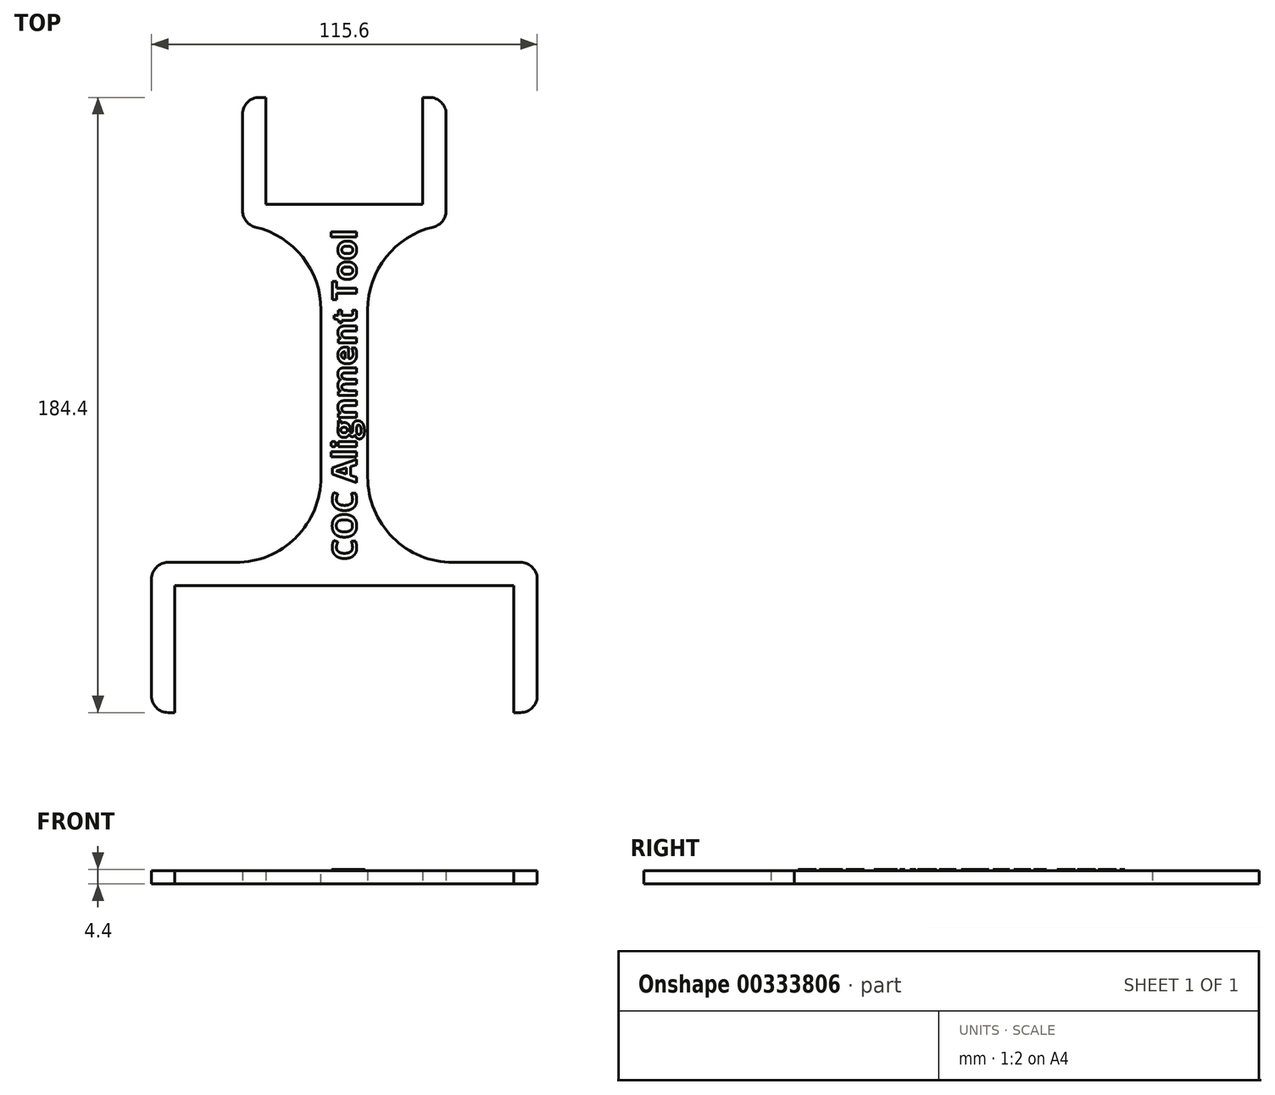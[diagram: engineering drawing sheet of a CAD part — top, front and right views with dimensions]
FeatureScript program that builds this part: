
annotation { "Feature Type Name" : "Feature", "Feature Type Description" : "" }
export const myFeature = defineFeature(function(context is Context, id is Id, definition is map)
    precondition{}
    {
        {
            var Q0;
            Q0=qCreatedBy(makeId("Top.planeOp"),FACE);
            var sketch = newSketch(context, id + "F0", { "sketchPlane" : qUnion([Q0])});
            skLineSegment(sketch, "E0", {"start": v(0, 0) * mm, "end": v(0, -57.2) * mm, "construction": true});
            skLineSegment(sketch, "E1", {"start": v(-50.8, -57.2) * mm, "end": v(50.8, -57.2) * mm});
            skLineSegment(sketch, "E2", {"start": v(-50.8, -57.2) * mm, "end": v(-50.8, -95.2) * mm});
            skLineSegment(sketch, "E3", {"start": v(50.8, -57.2) * mm, "end": v(50.8, -95.2) * mm});
            skLineSegment(sketch, "E4", {"start": v(0, 0) * mm, "end": v(0, 57.2) * mm, "construction": true});
            skLineSegment(sketch, "E5", {"start": v(-23.5, 57.2) * mm, "end": v(23.5, 57.2) * mm});
            skLineSegment(sketch, "E6", {"start": v(-23.5, 57.2) * mm, "end": v(-23.5, 89.2) * mm});
            skLineSegment(sketch, "E7", {"start": v(23.5, 57.2) * mm, "end": v(23.5, 89.2) * mm});
            skLineSegment(sketch, "E8", {"start": v(23.5, 89.2) * mm, "end": v(30.5, 89.2) * mm});
            skLineSegment(sketch, "E9", {"start": v(30.5, 89.2) * mm, "end": v(30.5, 57.2) * mm});
            skLineSegment(sketch, "E10", {"start": v(-23.5, 89.2) * mm, "end": v(-30.5, 89.2) * mm});
            skLineSegment(sketch, "E11", {"start": v(-50.8, -95.2) * mm, "end": v(-57.8, -95.2) * mm});
            skLineSegment(sketch, "E12", {"start": v(50.8, -95.2) * mm, "end": v(57.8, -95.2) * mm});
            skLineSegment(sketch, "E13", {"start": v(57.8, -95.2) * mm, "end": v(57.8, -57.2) * mm});
            skLineSegment(sketch, "E14", {"start": v(-57.8, -95.2) * mm, "end": v(-57.8, -57.2) * mm});
            skLineSegment(sketch, "E15", {"start": v(-30.5, 89.2) * mm, "end": v(-30.5, 57.2) * mm});
            skLineSegment(sketch, "E16", {"start": v(-30.5, 57.2) * mm, "end": v(-30.5, 50.2) * mm});
            skLineSegment(sketch, "E17", {"start": v(0, 50.2) * mm, "end": v(-7, 50.2) * mm, "construction": true});
            skLineSegment(sketch, "E18", {"start": v(-30.5, 50.2) * mm, "end": v(-7, 50.2) * mm});
            skLineSegment(sketch, "E19", {"start": v(0, 50.2) * mm, "end": v(7, 50.2) * mm, "construction": true});
            skLineSegment(sketch, "E20", {"start": v(7, 50.2) * mm, "end": v(30.5, 50.2) * mm});
            skLineSegment(sketch, "E21", {"start": v(30.5, 50.2) * mm, "end": v(30.5, 57.2) * mm});
            skLineSegment(sketch, "E22", {"start": v(-57.8, -57.2) * mm, "end": v(-57.8, -50.2) * mm});
            skLineSegment(sketch, "E23", {"start": v(-57.8, -50.2) * mm, "end": v(-7, -50.2) * mm});
            skLineSegment(sketch, "E24", {"start": v(-7, -50.2) * mm, "end": v(-7, 50.2) * mm});
            skLineSegment(sketch, "E25", {"start": v(57.8, -57.2) * mm, "end": v(57.8, -50.2) * mm});
            skLineSegment(sketch, "E26", {"start": v(57.8, -50.2) * mm, "end": v(7, -50.2) * mm});
            skLineSegment(sketch, "E27", {"start": v(7, -50.2) * mm, "end": v(7, 50.2) * mm});
            skLineSegment(sketch, "E28", {"start": v(-7, -50.2) * mm, "end": v(-22, -50.2) * mm, "construction": true});
            skLineSegment(sketch, "E29", {"start": v(-7, -50.2) * mm, "end": v(-7, -35.2) * mm, "construction": true});
            skLineSegment(sketch, "E30", {"start": v(-22, -50.2) * mm, "end": v(-7, -35.2) * mm});
            skLineSegment(sketch, "E31.MirrorCS", {"start": v(22, -50.2) * mm, "end": v(7, -35.2) * mm});
            skSolve(sketch);
        }
        {
            var Q0;
            Q0=makeQuery(id+"F0.imprint","IMPRINT",FACE,{"disambiguationData":[TD([[makeQuery(id+"F0.imprint","IMPRINT",EDGE,{"derivedFrom":sQuery(id+"F0.wireOp",EDGE,"E1")}),1.0]])]});
            var Q1;
            {var subQ3=sQuery(id+"F0.wireOp",EDGE,"E30");Q1=makeQuery(id+"F0.imprint","IMPRINT",FACE,{"disambiguationData":[TD([[makeQuery(id+"F0.imprint","IMPRINT",EDGE,{"derivedFrom":subQ3}),-1.0]])]});}
            var Q2;
            {var subQ3=sQuery(id+"F0.wireOp",EDGE,"E31.MirrorCS");Q2=makeQuery(id+"F0.imprint","IMPRINT",FACE,{"disambiguationData":[TD([[makeQuery(id+"F0.imprint","IMPRINT",EDGE,{"derivedFrom":subQ3}),1.0]])]});}
            extrude(context, id + "F1", {"entities" : qUnion([Q0, Q1, Q2]), "depth" : 4 * mm});
        }
        {
            var Q0;
            Q0=makeQuery(id+"F1.opExtrude","SWEPT_EDGE",EDGE,{"disambiguationData":[OSD([sQuery(id+"F0.wireOp",EDGE,"E22"),sQuery(id+"F0.wireOp",EDGE,"E23")])]});
            var Q1;
            Q1=makeQuery(id+"F1.opExtrude","SWEPT_EDGE",EDGE,{"disambiguationData":[OSD([sQuery(id+"F0.wireOp",EDGE,"E25"),sQuery(id+"F0.wireOp",EDGE,"E26")])]});
            var Q2;
            Q2=makeQuery(id+"F1.opExtrude","SWEPT_EDGE",EDGE,{"disambiguationData":[OSD([sQuery(id+"F0.wireOp",EDGE,"E20"),sQuery(id+"F0.wireOp",EDGE,"E21")])]});
            var Q3;
            Q3=makeQuery(id+"F1.opExtrude","SWEPT_EDGE",EDGE,{"disambiguationData":[OSD([sQuery(id+"F0.wireOp",EDGE,"E16"),sQuery(id+"F0.wireOp",EDGE,"E18")])]});
            var Q4;
            Q4=makeQuery(id+"F1.opExtrude","SWEPT_EDGE",EDGE,{"disambiguationData":[OSD([sQuery(id+"F0.wireOp",EDGE,"E11"),sQuery(id+"F0.wireOp",EDGE,"E14")])]});
            var Q5;
            Q5=makeQuery(id+"F1.opExtrude","SWEPT_EDGE",EDGE,{"disambiguationData":[OSD([sQuery(id+"F0.wireOp",EDGE,"E12"),sQuery(id+"F0.wireOp",EDGE,"E13")])]});
            var Q6;
            Q6=makeQuery(id+"F1.opExtrude","SWEPT_EDGE",EDGE,{"disambiguationData":[OSD([sQuery(id+"F0.wireOp",EDGE,"E8"),sQuery(id+"F0.wireOp",EDGE,"E9")])]});
            var Q7;
            Q7=makeQuery(id+"F1.opExtrude","SWEPT_EDGE",EDGE,{"disambiguationData":[OSD([sQuery(id+"F0.wireOp",EDGE,"E10"),sQuery(id+"F0.wireOp",EDGE,"E15")])]});
            fillet(context, id + "F2", {"entities" : qUnion([Q0, Q1, Q2, Q3, Q4, Q5, Q6, Q7]), "radius" : 5 * mm, "tangentPropagation" : true, "allowEdgeOverflow" : false});
        }
        {
            var Q0;
            Q0=makeQuery(id+"F1.opExtrude","SWEPT_EDGE",EDGE,{"disambiguationData":[OSD([sQuery(id+"F0.wireOp",EDGE,"E24"),sQuery(id+"F0.wireOp",EDGE,"E30")])]});
            var Q1;
            Q1=makeQuery(id+"F1.opExtrude","SWEPT_EDGE",EDGE,{"disambiguationData":[OSD([sQuery(id+"F0.wireOp",EDGE,"E23"),sQuery(id+"F0.wireOp",EDGE,"E30")])]});
            var Q2;
            Q2=makeQuery(id+"F1.opExtrude","SWEPT_EDGE",EDGE,{"disambiguationData":[OSD([sQuery(id+"F0.wireOp",EDGE,"E26"),sQuery(id+"F0.wireOp",EDGE,"E31.MirrorCS")])]});
            var Q3;
            Q3=makeQuery(id+"F1.opExtrude","SWEPT_EDGE",EDGE,{"disambiguationData":[OSD([sQuery(id+"F0.wireOp",EDGE,"E27"),sQuery(id+"F0.wireOp",EDGE,"E31.MirrorCS")])]});
            var Q4;
            Q4=makeQuery(id+"F1.opExtrude","SWEPT_EDGE",EDGE,{"disambiguationData":[OSD([sQuery(id+"F0.wireOp",EDGE,"E18"),sQuery(id+"F0.wireOp",EDGE,"E24")])]});
            var Q5;
            Q5=makeQuery(id+"F1.opExtrude","SWEPT_EDGE",EDGE,{"disambiguationData":[OSD([sQuery(id+"F0.wireOp",EDGE,"E20"),sQuery(id+"F0.wireOp",EDGE,"E27")])]});
            fillet(context, id + "F3", {"entities" : qUnion([Q0, Q1, Q2, Q3, Q4, Q5]), "radius" : 25.49 * mm, "tangentPropagation" : true, "allowEdgeOverflow" : false});
        }
        {
            var Q0;
            Q0=makeQuery(id+"F1.opExtrude","CAP_FACE",FACE,{"disambiguationData":[OSD([sQuery(id+"F0.wireOp",EDGE,"E1"),sQuery(id+"F0.wireOp",EDGE,"E2"),sQuery(id+"F0.wireOp",EDGE,"E3"),sQuery(id+"F0.wireOp",EDGE,"E5"),sQuery(id+"F0.wireOp",EDGE,"E6"),sQuery(id+"F0.wireOp",EDGE,"E7"),sQuery(id+"F0.wireOp",EDGE,"E8"),sQuery(id+"F0.wireOp",EDGE,"E9"),sQuery(id+"F0.wireOp",EDGE,"E10"),sQuery(id+"F0.wireOp",EDGE,"E11"),sQuery(id+"F0.wireOp",EDGE,"E12"),sQuery(id+"F0.wireOp",EDGE,"E13"),sQuery(id+"F0.wireOp",EDGE,"E14"),sQuery(id+"F0.wireOp",EDGE,"E15"),sQuery(id+"F0.wireOp",EDGE,"E16"),sQuery(id+"F0.wireOp",EDGE,"E18"),sQuery(id+"F0.wireOp",EDGE,"E20"),sQuery(id+"F0.wireOp",EDGE,"E21"),sQuery(id+"F0.wireOp",EDGE,"E22"),sQuery(id+"F0.wireOp",EDGE,"E23"),sQuery(id+"F0.wireOp",EDGE,"E24"),sQuery(id+"F0.wireOp",EDGE,"E25"),sQuery(id+"F0.wireOp",EDGE,"E26"),sQuery(id+"F0.wireOp",EDGE,"E27"),sQuery(id+"F0.wireOp",EDGE,"E30"),sQuery(id+"F0.wireOp",EDGE,"E31.MirrorCS")])],"isStart":false});
            var sketch = newSketch(context, id + "F4", { "sketchPlane" : qUnion([Q0])});
            skText(sketch, "E32", { "text": "COC Alignment Tool", "fontName": "OpenSans-Bold.ttf"});
            skLineSegment(sketch, "E33", {"start": v(-7, 0.44) * mm, "end": v(-7, -57.2) * mm, "construction": true});
            skLineSegment(sketch, "E34", {"start": v(7, 0.44) * mm, "end": v(7, -57.2) * mm, "construction": true});
            skLineSegment(sketch, "E35", {"start": v(7, 0.44) * mm, "end": v(7, 57.2) * mm, "construction": true});
            skLineSegment(sketch, "E36", {"start": v(-7, 0.44) * mm, "end": v(-7, 57.2) * mm, "construction": true});
            const initialGuessF4  = {"E32": [0.00361, -0.0496, 0, 1, 0.00722]};
            skSetInitialGuess(sketch, initialGuessF4);
            skSolve(sketch);
        }
        {
            var Q0;
            Q0 = qSketchRegion(id + "F4", true);
            extrude(context, id + "F5", {"entities" : qUnion([Q0]), "operationType" : NewBodyOperationType.ADD, "depth" : .4 * mm});
        }
    });
